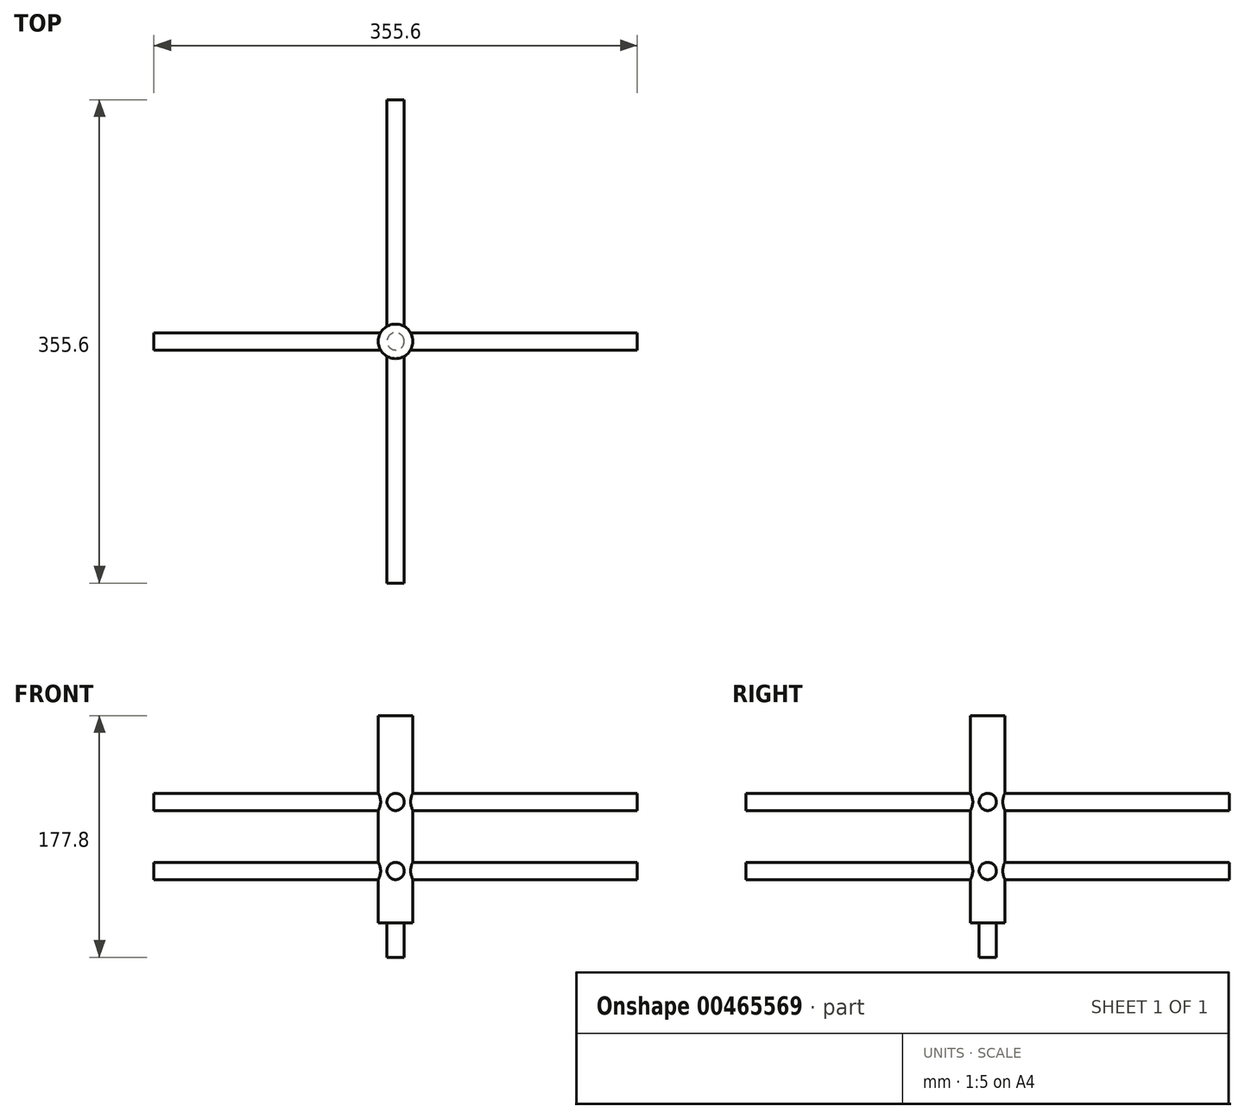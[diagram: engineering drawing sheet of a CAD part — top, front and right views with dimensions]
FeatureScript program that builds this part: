
annotation { "Feature Type Name" : "Feature", "Feature Type Description" : "" }
export const myFeature = defineFeature(function(context is Context, id is Id, definition is map)
    precondition{}
    {
        {
            var Q0;
            Q0=qCreatedBy(makeId("Top.planeOp"),FACE);
            var sketch = newSketch(context, id + "F0", { "sketchPlane" : qUnion([Q0])});
            skCircle(sketch, "E0", {"center": v(0, 0) * mm, "radius": 12.7 * mm});
            skSolve(sketch);
        }
        {
            var Q0;
            Q0 = qSketchRegion(id + "F0", true);
            extrude(context, id + "F1", {"entities" : qUnion([Q0]), "depth" : 152.4 * mm});
        }
        {
            var Q0;
            Q0=makeQuery(id+"F1.opExtrude","CAP_FACE",FACE,{"disambiguationData":[OSD([sQuery(id+"F0.wireOp",EDGE,"E0")])],"isStart":true});
            var sketch = newSketch(context, id + "F2", { "sketchPlane" : qUnion([Q0])});
            skCircle(sketch, "E1", {"center": v(0, 0) * mm, "radius": 6.35 * mm});
            skSolve(sketch);
        }
        {
            var Q0;
            Q0 = qSketchRegion(id + "F2", true);
            extrude(context, id + "F3", {"entities" : qUnion([Q0]), "operationType" : NewBodyOperationType.ADD, "depth" : 25.4 * mm});
        }
        {
            var Q0;
            Q0=qCreatedBy(makeId("Front.planeOp"),FACE);
            var sketch = newSketch(context, id + "F4", { "sketchPlane" : qUnion([Q0])});
            skCircle(sketch, "E2", {"center": v(0, 88.9) * mm, "radius": 6.35 * mm});
            skSolve(sketch);
        }
        {
            var Q0;
            Q0=qCreatedBy(makeId("Front.planeOp"),FACE);
            var sketch = newSketch(context, id + "F5", { "sketchPlane" : qUnion([Q0])});
            skCircle(sketch, "E3", {"center": v(0, 38.1) * mm, "radius": 6.35 * mm});
            skSolve(sketch);
        }
        {
            var Q0;
            Q0 = qSketchRegion(id + "F5", true);
            var Q1;
            Q1 = qSketchRegion(id + "F4", true);
            extrude(context, id + "F6", {"entities" : qUnion([Q0, Q1]), "operationType" : NewBodyOperationType.ADD, "depth" : 355.6 * mm, "symmetric" : true});
        }
        {
            var Q0;
            Q0=qCreatedBy(makeId("Right.planeOp"),FACE);
            var sketch = newSketch(context, id + "F7", { "sketchPlane" : qUnion([Q0])});
            skCircle(sketch, "E4", {"center": v(0, 38.1) * mm, "radius": 6.35 * mm});
            skCircle(sketch, "E5", {"center": v(0, 88.9) * mm, "radius": 6.35 * mm});
            skSolve(sketch);
        }
        {
            var Q0;
            Q0 = qSketchRegion(id + "F7", true);
            extrude(context, id + "F8", {"entities" : qUnion([Q0]), "operationType" : NewBodyOperationType.ADD, "depth" : 355.6 * mm, "symmetric" : true});
        }
    });
